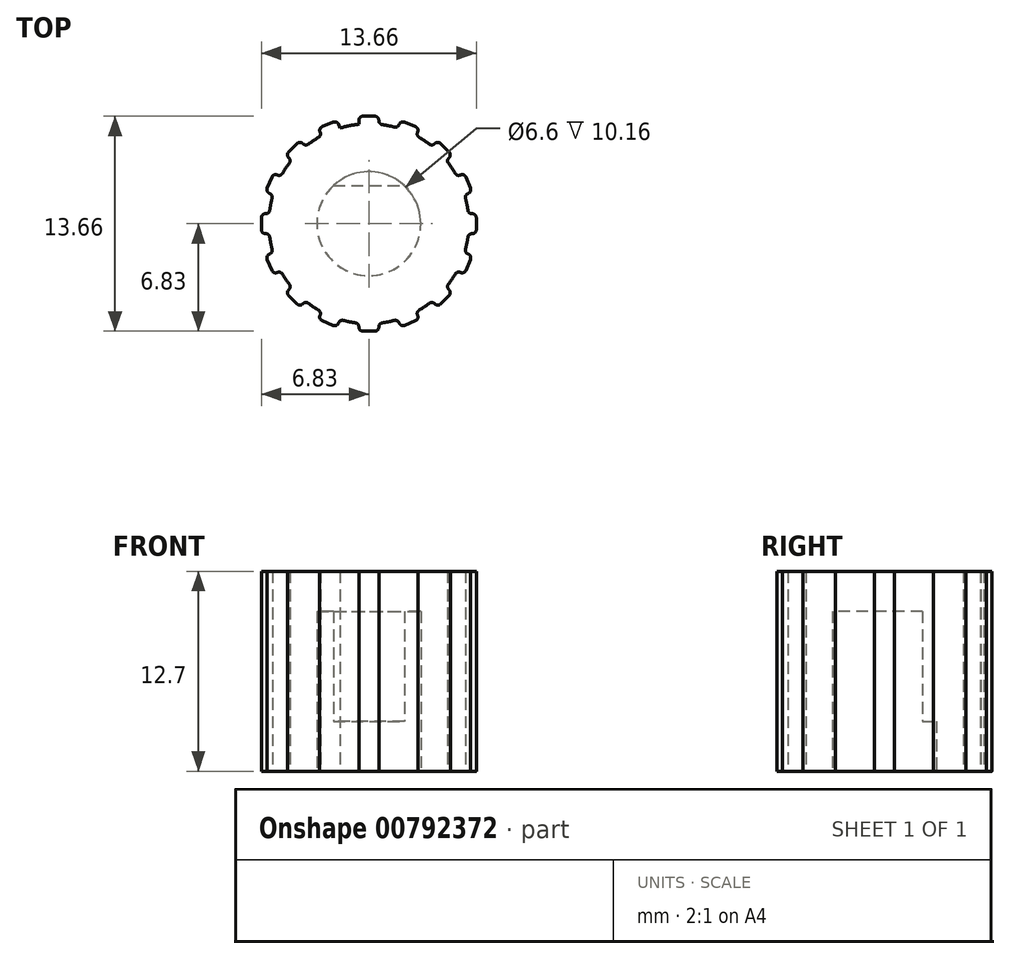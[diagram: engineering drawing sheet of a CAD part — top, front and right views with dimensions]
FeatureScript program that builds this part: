
annotation { "Feature Type Name" : "Feature", "Feature Type Description" : "" }
export const myFeature = defineFeature(function(context is Context, id is Id, definition is map)
    precondition{}
    {
        {
            var Q0;
            Q0=qCreatedBy(makeId("Top.planeOp"),FACE);
            var sketch = newSketch(context, id + "F0", { "sketchPlane" : qUnion([Q0])});
            skCircle(sketch, "E0", {"center": v(0, 0) * mm, "radius": 6.35 * mm});
            skSolve(sketch);
        }
        {
            var Q0;
            Q0 = qSketchRegion(id + "F0", true);
            extrude(context, id + "F1", {"entities" : qUnion([Q0]), "depth" : 12.7 * mm, "offsetDistance" : 25.4 * mm});
        }
        {
            var Q0;
            Q0=qCreatedBy(makeId("Top.planeOp"),FACE);
            var sketch = newSketch(context, id + "F2", { "sketchPlane" : qUnion([Q0])});
            skLineSegment(sketch, "E1", {"start": v(-0.63, 6.32) * mm, "end": v(-0.64, 6.83) * mm});
            skLineSegment(sketch, "E2", {"start": v(-0.64, 6.83) * mm, "end": v(0.64, 6.83) * mm});
            skLineSegment(sketch, "E3", {"start": v(0.64, 6.83) * mm, "end": v(0.64, 6.32) * mm});
            skLineSegment(sketch, "E4", {"start": v(0.64, 6.32) * mm, "end": v(-0.64, 6.32) * mm});
            skLineSegment(sketch, "E5.1.0", {"start": v(-3.2, 6.06) * mm, "end": v(-2.03, 6.55) * mm});
            skLineSegment(sketch, "E5.1.1", {"start": v(-3, 5.6) * mm, "end": v(-3.2, 6.06) * mm});
            skLineSegment(sketch, "E5.1.2", {"start": v(-1.83, 6.08) * mm, "end": v(-3, 5.6) * mm});
            skLineSegment(sketch, "E5.1.3", {"start": v(-2.03, 6.55) * mm, "end": v(-1.83, 6.08) * mm});
            skLineSegment(sketch, "E5.2.0", {"start": v(-5.28, 4.38) * mm, "end": v(-4.38, 5.28) * mm});
            skLineSegment(sketch, "E5.2.1", {"start": v(-4.92, 4.02) * mm, "end": v(-5.28, 4.38) * mm});
            skLineSegment(sketch, "E5.2.2", {"start": v(-4.02, 4.92) * mm, "end": v(-4.92, 4.02) * mm});
            skLineSegment(sketch, "E5.2.3", {"start": v(-4.38, 5.28) * mm, "end": v(-4.02, 4.92) * mm});
            skLineSegment(sketch, "E5.3.0", {"start": v(-6.55, 2.03) * mm, "end": v(-6.06, 3.2) * mm});
            skLineSegment(sketch, "E5.3.1", {"start": v(-6.08, 1.83) * mm, "end": v(-6.55, 2.03) * mm});
            skLineSegment(sketch, "E5.3.2", {"start": v(-5.6, 3) * mm, "end": v(-6.08, 1.83) * mm});
            skLineSegment(sketch, "E5.3.3", {"start": v(-6.06, 3.2) * mm, "end": v(-5.6, 3) * mm});
            skLineSegment(sketch, "E5.4.0", {"start": v(-6.83, -0.63) * mm, "end": v(-6.83, 0.64) * mm});
            skLineSegment(sketch, "E5.4.1", {"start": v(-6.32, -0.63) * mm, "end": v(-6.83, -0.63) * mm});
            skLineSegment(sketch, "E5.4.2", {"start": v(-6.32, 0.64) * mm, "end": v(-6.32, -0.63) * mm});
            skLineSegment(sketch, "E5.4.3", {"start": v(-6.83, 0.64) * mm, "end": v(-6.32, 0.64) * mm});
            skLineSegment(sketch, "E5.5.0", {"start": v(-6.06, -3.2) * mm, "end": v(-6.55, -2.03) * mm});
            skLineSegment(sketch, "E5.5.1", {"start": v(-5.6, -3) * mm, "end": v(-6.06, -3.2) * mm});
            skLineSegment(sketch, "E5.5.2", {"start": v(-6.08, -1.83) * mm, "end": v(-5.6, -3) * mm});
            skLineSegment(sketch, "E5.5.3", {"start": v(-6.55, -2.03) * mm, "end": v(-6.08, -1.83) * mm});
            skLineSegment(sketch, "E5.6.0", {"start": v(-4.38, -5.28) * mm, "end": v(-5.28, -4.38) * mm});
            skLineSegment(sketch, "E5.6.1", {"start": v(-4.02, -4.92) * mm, "end": v(-4.38, -5.28) * mm});
            skLineSegment(sketch, "E5.6.2", {"start": v(-4.92, -4.02) * mm, "end": v(-4.02, -4.92) * mm});
            skLineSegment(sketch, "E5.6.3", {"start": v(-5.28, -4.38) * mm, "end": v(-4.92, -4.02) * mm});
            skLineSegment(sketch, "E5.7.0", {"start": v(-2.03, -6.55) * mm, "end": v(-3.2, -6.06) * mm});
            skLineSegment(sketch, "E5.7.1", {"start": v(-1.83, -6.08) * mm, "end": v(-2.03, -6.55) * mm});
            skLineSegment(sketch, "E5.7.2", {"start": v(-3, -5.6) * mm, "end": v(-1.83, -6.08) * mm});
            skLineSegment(sketch, "E5.7.3", {"start": v(-3.2, -6.06) * mm, "end": v(-3, -5.6) * mm});
            skLineSegment(sketch, "E5.8.0", {"start": v(0.63, -6.83) * mm, "end": v(-0.64, -6.83) * mm});
            skLineSegment(sketch, "E5.8.1", {"start": v(0.63, -6.32) * mm, "end": v(0.63, -6.83) * mm});
            skLineSegment(sketch, "E5.8.2", {"start": v(-0.64, -6.32) * mm, "end": v(0.63, -6.32) * mm});
            skLineSegment(sketch, "E5.8.3", {"start": v(-0.64, -6.83) * mm, "end": v(-0.64, -6.32) * mm});
            skLineSegment(sketch, "E5.9.0", {"start": v(3.2, -6.06) * mm, "end": v(2.03, -6.55) * mm});
            skLineSegment(sketch, "E5.9.1", {"start": v(3, -5.6) * mm, "end": v(3.2, -6.06) * mm});
            skLineSegment(sketch, "E5.9.2", {"start": v(1.83, -6.08) * mm, "end": v(3, -5.6) * mm});
            skLineSegment(sketch, "E5.9.3", {"start": v(2.03, -6.55) * mm, "end": v(1.83, -6.08) * mm});
            skLineSegment(sketch, "E5.10.0", {"start": v(5.28, -4.38) * mm, "end": v(4.38, -5.28) * mm});
            skLineSegment(sketch, "E5.10.1", {"start": v(4.92, -4.02) * mm, "end": v(5.28, -4.38) * mm});
            skLineSegment(sketch, "E5.10.2", {"start": v(4.02, -4.92) * mm, "end": v(4.92, -4.02) * mm});
            skLineSegment(sketch, "E5.10.3", {"start": v(4.38, -5.28) * mm, "end": v(4.02, -4.92) * mm});
            skLineSegment(sketch, "E5.11.0", {"start": v(6.55, -2.03) * mm, "end": v(6.06, -3.2) * mm});
            skLineSegment(sketch, "E5.11.1", {"start": v(6.08, -1.83) * mm, "end": v(6.55, -2.03) * mm});
            skLineSegment(sketch, "E5.11.2", {"start": v(5.6, -3) * mm, "end": v(6.08, -1.83) * mm});
            skLineSegment(sketch, "E5.11.3", {"start": v(6.06, -3.2) * mm, "end": v(5.6, -3) * mm});
            skLineSegment(sketch, "E5.12.0", {"start": v(6.83, 0.63) * mm, "end": v(6.83, -0.64) * mm});
            skLineSegment(sketch, "E5.12.1", {"start": v(6.32, 0.63) * mm, "end": v(6.83, 0.63) * mm});
            skLineSegment(sketch, "E5.12.2", {"start": v(6.32, -0.64) * mm, "end": v(6.32, 0.63) * mm});
            skLineSegment(sketch, "E5.12.3", {"start": v(6.83, -0.64) * mm, "end": v(6.32, -0.64) * mm});
            skLineSegment(sketch, "E5.13.0", {"start": v(6.06, 3.2) * mm, "end": v(6.55, 2.03) * mm});
            skLineSegment(sketch, "E5.13.1", {"start": v(5.6, 3) * mm, "end": v(6.06, 3.2) * mm});
            skLineSegment(sketch, "E5.13.2", {"start": v(6.08, 1.83) * mm, "end": v(5.6, 3) * mm});
            skLineSegment(sketch, "E5.13.3", {"start": v(6.55, 2.03) * mm, "end": v(6.08, 1.83) * mm});
            skLineSegment(sketch, "E5.14.0", {"start": v(4.38, 5.28) * mm, "end": v(5.28, 4.38) * mm});
            skLineSegment(sketch, "E5.14.1", {"start": v(4.02, 4.92) * mm, "end": v(4.38, 5.28) * mm});
            skLineSegment(sketch, "E5.14.2", {"start": v(4.92, 4.02) * mm, "end": v(4.02, 4.92) * mm});
            skLineSegment(sketch, "E5.14.3", {"start": v(5.28, 4.38) * mm, "end": v(4.92, 4.02) * mm});
            skLineSegment(sketch, "E5.15.0", {"start": v(2.03, 6.55) * mm, "end": v(3.2, 6.06) * mm});
            skLineSegment(sketch, "E5.15.1", {"start": v(1.83, 6.08) * mm, "end": v(2.03, 6.55) * mm});
            skLineSegment(sketch, "E5.15.2", {"start": v(3, 5.6) * mm, "end": v(1.83, 6.08) * mm});
            skLineSegment(sketch, "E5.15.3", {"start": v(3.2, 6.06) * mm, "end": v(3, 5.6) * mm});
            skPoint(sketch, "E5.center", {"position": v(0, 0) * mm});
            skSolve(sketch);
        }
        {
            var Q0;
            Q0 = qSketchRegion(id + "F2", true);
            var Q1;
            Q1=makeQuery(id+"F1.opExtrude","CAP_FACE",FACE,{"disambiguationData":[OSD([sQuery(id+"F0.wireOp",EDGE,"E0")])],"isStart":false});
            extrude(context, id + "F3", {"entities" : qUnion([Q0]), "operationType" : NewBodyOperationType.ADD, "endBound" : BoundingType.UP_TO_SURFACE, "depth" : 25.4 * mm, "endBoundEntityFace" : qUnion([Q1]), "offsetDistance" : 25.4 * mm});
        }
        {
            var Q0;
            Q0=makeQuery(id+"F3.opExtrude","SWEPT_EDGE",EDGE,{"disambiguationData":[OSD([sQuery(id+"F2.wireOp",EDGE,"E2"),sQuery(id+"F2.wireOp",EDGE,"E3")])]});
            var Q1;
            Q1=makeQuery(id+"F3.opExtrude","SWEPT_EDGE",EDGE,{"disambiguationData":[OSD([sQuery(id+"F2.wireOp",EDGE,"E1"),sQuery(id+"F2.wireOp",EDGE,"E2")])]});
            var Q2;
            Q2=makeQuery(id+"F3.opExtrude","SWEPT_EDGE",EDGE,{"disambiguationData":[OSD([sQuery(id+"F2.wireOp",EDGE,"E3"),sQuery(id+"F2.wireOp",EDGE,"E4")])]});
            var Q3;
            Q3=makeQuery(id+"F3.opExtrude","SWEPT_EDGE",EDGE,{"disambiguationData":[OSD([sQuery(id+"F2.wireOp",EDGE,"E1"),sQuery(id+"F2.wireOp",EDGE,"E4")])]});
            var Q4;
            Q4=makeQuery(id+"F3.opExtrude","SWEPT_EDGE",EDGE,{"disambiguationData":[OSD([sQuery(id+"F2.wireOp",EDGE,"E5.15.1"),sQuery(id+"F2.wireOp",EDGE,"E5.15.2")])]});
            var Q5;
            Q5=makeQuery(id+"F3.opExtrude","SWEPT_EDGE",EDGE,{"disambiguationData":[OSD([sQuery(id+"F2.wireOp",EDGE,"E5.15.0"),sQuery(id+"F2.wireOp",EDGE,"E5.15.1")])]});
            var Q6;
            Q6=makeQuery(id+"F3.opExtrude","SWEPT_EDGE",EDGE,{"disambiguationData":[OSD([sQuery(id+"F2.wireOp",EDGE,"E5.15.0"),sQuery(id+"F2.wireOp",EDGE,"E5.15.3")])]});
            var Q7;
            Q7=makeQuery(id+"F3.opExtrude","SWEPT_EDGE",EDGE,{"disambiguationData":[OSD([sQuery(id+"F2.wireOp",EDGE,"E5.15.2"),sQuery(id+"F2.wireOp",EDGE,"E5.15.3")])]});
            var Q8;
            Q8=makeQuery(id+"F3.opExtrude","SWEPT_EDGE",EDGE,{"disambiguationData":[OSD([sQuery(id+"F2.wireOp",EDGE,"E5.14.0"),sQuery(id+"F2.wireOp",EDGE,"E5.14.1")])]});
            var Q9;
            Q9=makeQuery(id+"F3.opExtrude","SWEPT_EDGE",EDGE,{"disambiguationData":[OSD([sQuery(id+"F2.wireOp",EDGE,"E5.14.0"),sQuery(id+"F2.wireOp",EDGE,"E5.14.3")])]});
            var Q10;
            Q10=makeQuery(id+"F3.opExtrude","SWEPT_EDGE",EDGE,{"disambiguationData":[OSD([sQuery(id+"F2.wireOp",EDGE,"E5.14.1"),sQuery(id+"F2.wireOp",EDGE,"E5.14.2")])]});
            var Q11;
            Q11=makeQuery(id+"F3.opExtrude","SWEPT_EDGE",EDGE,{"disambiguationData":[OSD([sQuery(id+"F2.wireOp",EDGE,"E5.14.2"),sQuery(id+"F2.wireOp",EDGE,"E5.14.3")])]});
            var Q12;
            Q12=makeQuery(id+"F3.opExtrude","SWEPT_EDGE",EDGE,{"disambiguationData":[OSD([sQuery(id+"F2.wireOp",EDGE,"E5.13.1"),sQuery(id+"F2.wireOp",EDGE,"E5.13.2")])]});
            var Q13;
            Q13=makeQuery(id+"F3.opExtrude","SWEPT_EDGE",EDGE,{"disambiguationData":[OSD([sQuery(id+"F2.wireOp",EDGE,"E5.13.0"),sQuery(id+"F2.wireOp",EDGE,"E5.13.1")])]});
            var Q14;
            Q14=makeQuery(id+"F3.opExtrude","SWEPT_EDGE",EDGE,{"disambiguationData":[OSD([sQuery(id+"F2.wireOp",EDGE,"E5.13.0"),sQuery(id+"F2.wireOp",EDGE,"E5.13.3")])]});
            var Q15;
            Q15=makeQuery(id+"F3.opExtrude","SWEPT_EDGE",EDGE,{"disambiguationData":[OSD([sQuery(id+"F2.wireOp",EDGE,"E5.13.2"),sQuery(id+"F2.wireOp",EDGE,"E5.13.3")])]});
            var Q16;
            Q16=makeQuery(id+"F3.opExtrude","SWEPT_EDGE",EDGE,{"disambiguationData":[OSD([sQuery(id+"F2.wireOp",EDGE,"E5.12.0"),sQuery(id+"F2.wireOp",EDGE,"E5.12.1")])]});
            var Q17;
            Q17=makeQuery(id+"F3.opExtrude","SWEPT_EDGE",EDGE,{"disambiguationData":[OSD([sQuery(id+"F2.wireOp",EDGE,"E5.12.1"),sQuery(id+"F2.wireOp",EDGE,"E5.12.2")])]});
            var Q18;
            Q18=makeQuery(id+"F3.opExtrude","SWEPT_EDGE",EDGE,{"disambiguationData":[OSD([sQuery(id+"F2.wireOp",EDGE,"E5.12.0"),sQuery(id+"F2.wireOp",EDGE,"E5.12.3")])]});
            var Q19;
            Q19=makeQuery(id+"F3.opExtrude","SWEPT_EDGE",EDGE,{"disambiguationData":[OSD([sQuery(id+"F2.wireOp",EDGE,"E5.12.2"),sQuery(id+"F2.wireOp",EDGE,"E5.12.3")])]});
            var Q20;
            Q20=makeQuery(id+"F3.opExtrude","SWEPT_EDGE",EDGE,{"disambiguationData":[OSD([sQuery(id+"F2.wireOp",EDGE,"E5.11.0"),sQuery(id+"F2.wireOp",EDGE,"E5.11.1")])]});
            var Q21;
            Q21=makeQuery(id+"F3.opExtrude","SWEPT_EDGE",EDGE,{"disambiguationData":[OSD([sQuery(id+"F2.wireOp",EDGE,"E5.11.1"),sQuery(id+"F2.wireOp",EDGE,"E5.11.2")])]});
            var Q22;
            Q22=makeQuery(id+"F3.opExtrude","SWEPT_EDGE",EDGE,{"disambiguationData":[OSD([sQuery(id+"F2.wireOp",EDGE,"E5.11.0"),sQuery(id+"F2.wireOp",EDGE,"E5.11.3")])]});
            var Q23;
            Q23=makeQuery(id+"F3.opExtrude","SWEPT_EDGE",EDGE,{"disambiguationData":[OSD([sQuery(id+"F2.wireOp",EDGE,"E5.10.0"),sQuery(id+"F2.wireOp",EDGE,"E5.10.1")])]});
            var Q24;
            Q24=makeQuery(id+"F3.opExtrude","SWEPT_EDGE",EDGE,{"disambiguationData":[OSD([sQuery(id+"F2.wireOp",EDGE,"E5.11.2"),sQuery(id+"F2.wireOp",EDGE,"E5.11.3")])]});
            var Q25;
            Q25=makeQuery(id+"F3.opExtrude","SWEPT_EDGE",EDGE,{"disambiguationData":[OSD([sQuery(id+"F2.wireOp",EDGE,"E5.10.1"),sQuery(id+"F2.wireOp",EDGE,"E5.10.2")])]});
            var Q26;
            Q26=makeQuery(id+"F3.opExtrude","SWEPT_EDGE",EDGE,{"disambiguationData":[OSD([sQuery(id+"F2.wireOp",EDGE,"E5.10.0"),sQuery(id+"F2.wireOp",EDGE,"E5.10.3")])]});
            var Q27;
            Q27=makeQuery(id+"F3.opExtrude","SWEPT_EDGE",EDGE,{"disambiguationData":[OSD([sQuery(id+"F2.wireOp",EDGE,"E5.10.2"),sQuery(id+"F2.wireOp",EDGE,"E5.10.3")])]});
            var Q28;
            Q28=makeQuery(id+"F3.opExtrude","SWEPT_EDGE",EDGE,{"disambiguationData":[OSD([sQuery(id+"F2.wireOp",EDGE,"E5.9.1"),sQuery(id+"F2.wireOp",EDGE,"E5.9.2")])]});
            var Q29;
            Q29=makeQuery(id+"F3.opExtrude","SWEPT_EDGE",EDGE,{"disambiguationData":[OSD([sQuery(id+"F2.wireOp",EDGE,"E5.9.0"),sQuery(id+"F2.wireOp",EDGE,"E5.9.1")])]});
            var Q30;
            Q30=makeQuery(id+"F3.opExtrude","SWEPT_EDGE",EDGE,{"disambiguationData":[OSD([sQuery(id+"F2.wireOp",EDGE,"E5.8.1"),sQuery(id+"F2.wireOp",EDGE,"E5.8.2")])]});
            var Q31;
            Q31=makeQuery(id+"F3.opExtrude","SWEPT_EDGE",EDGE,{"disambiguationData":[OSD([sQuery(id+"F2.wireOp",EDGE,"E5.8.0"),sQuery(id+"F2.wireOp",EDGE,"E5.8.1")])]});
            var Q32;
            Q32=makeQuery(id+"F3.opExtrude","SWEPT_EDGE",EDGE,{"disambiguationData":[OSD([sQuery(id+"F2.wireOp",EDGE,"E5.9.2"),sQuery(id+"F2.wireOp",EDGE,"E5.9.3")])]});
            var Q33;
            Q33=makeQuery(id+"F3.opExtrude","SWEPT_EDGE",EDGE,{"disambiguationData":[OSD([sQuery(id+"F2.wireOp",EDGE,"E5.9.0"),sQuery(id+"F2.wireOp",EDGE,"E5.9.3")])]});
            var Q34;
            Q34=makeQuery(id+"F3.opExtrude","SWEPT_EDGE",EDGE,{"disambiguationData":[OSD([sQuery(id+"F2.wireOp",EDGE,"E5.8.0"),sQuery(id+"F2.wireOp",EDGE,"E5.8.3")])]});
            var Q35;
            Q35=makeQuery(id+"F3.opExtrude","SWEPT_EDGE",EDGE,{"disambiguationData":[OSD([sQuery(id+"F2.wireOp",EDGE,"E5.8.2"),sQuery(id+"F2.wireOp",EDGE,"E5.8.3")])]});
            var Q36;
            Q36=makeQuery(id+"F3.opExtrude","SWEPT_EDGE",EDGE,{"disambiguationData":[OSD([sQuery(id+"F2.wireOp",EDGE,"E5.7.1"),sQuery(id+"F2.wireOp",EDGE,"E5.7.2")])]});
            var Q37;
            Q37=makeQuery(id+"F3.opExtrude","SWEPT_EDGE",EDGE,{"disambiguationData":[OSD([sQuery(id+"F2.wireOp",EDGE,"E5.7.0"),sQuery(id+"F2.wireOp",EDGE,"E5.7.1")])]});
            var Q38;
            Q38=makeQuery(id+"F3.opExtrude","SWEPT_EDGE",EDGE,{"disambiguationData":[OSD([sQuery(id+"F2.wireOp",EDGE,"E5.7.0"),sQuery(id+"F2.wireOp",EDGE,"E5.7.3")])]});
            var Q39;
            Q39=makeQuery(id+"F3.opExtrude","SWEPT_EDGE",EDGE,{"disambiguationData":[OSD([sQuery(id+"F2.wireOp",EDGE,"E5.7.2"),sQuery(id+"F2.wireOp",EDGE,"E5.7.3")])]});
            var Q40;
            Q40=makeQuery(id+"F3.opExtrude","SWEPT_EDGE",EDGE,{"disambiguationData":[OSD([sQuery(id+"F2.wireOp",EDGE,"E5.6.1"),sQuery(id+"F2.wireOp",EDGE,"E5.6.2")])]});
            var Q41;
            Q41=makeQuery(id+"F3.opExtrude","SWEPT_EDGE",EDGE,{"disambiguationData":[OSD([sQuery(id+"F2.wireOp",EDGE,"E5.6.0"),sQuery(id+"F2.wireOp",EDGE,"E5.6.1")])]});
            var Q42;
            Q42=makeQuery(id+"F3.opExtrude","SWEPT_EDGE",EDGE,{"disambiguationData":[OSD([sQuery(id+"F2.wireOp",EDGE,"E5.5.1"),sQuery(id+"F2.wireOp",EDGE,"E5.5.2")])]});
            var Q43;
            Q43=makeQuery(id+"F3.opExtrude","SWEPT_EDGE",EDGE,{"disambiguationData":[OSD([sQuery(id+"F2.wireOp",EDGE,"E5.5.0"),sQuery(id+"F2.wireOp",EDGE,"E5.5.1")])]});
            var Q44;
            Q44=makeQuery(id+"F3.opExtrude","SWEPT_EDGE",EDGE,{"disambiguationData":[OSD([sQuery(id+"F2.wireOp",EDGE,"E5.6.0"),sQuery(id+"F2.wireOp",EDGE,"E5.6.3")])]});
            var Q45;
            Q45=makeQuery(id+"F3.opExtrude","SWEPT_EDGE",EDGE,{"disambiguationData":[OSD([sQuery(id+"F2.wireOp",EDGE,"E5.6.2"),sQuery(id+"F2.wireOp",EDGE,"E5.6.3")])]});
            var Q46;
            Q46=makeQuery(id+"F3.opExtrude","SWEPT_EDGE",EDGE,{"disambiguationData":[OSD([sQuery(id+"F2.wireOp",EDGE,"E5.5.2"),sQuery(id+"F2.wireOp",EDGE,"E5.5.3")])]});
            var Q47;
            Q47=makeQuery(id+"F3.opExtrude","SWEPT_EDGE",EDGE,{"disambiguationData":[OSD([sQuery(id+"F2.wireOp",EDGE,"E5.5.0"),sQuery(id+"F2.wireOp",EDGE,"E5.5.3")])]});
            var Q48;
            Q48=makeQuery(id+"F3.opExtrude","SWEPT_EDGE",EDGE,{"disambiguationData":[OSD([sQuery(id+"F2.wireOp",EDGE,"E5.4.1"),sQuery(id+"F2.wireOp",EDGE,"E5.4.2")])]});
            var Q49;
            Q49=makeQuery(id+"F3.opExtrude","SWEPT_EDGE",EDGE,{"disambiguationData":[OSD([sQuery(id+"F2.wireOp",EDGE,"E5.4.0"),sQuery(id+"F2.wireOp",EDGE,"E5.4.1")])]});
            var Q50;
            Q50=makeQuery(id+"F3.opExtrude","SWEPT_EDGE",EDGE,{"disambiguationData":[OSD([sQuery(id+"F2.wireOp",EDGE,"E5.4.0"),sQuery(id+"F2.wireOp",EDGE,"E5.4.3")])]});
            var Q51;
            Q51=makeQuery(id+"F3.opExtrude","SWEPT_EDGE",EDGE,{"disambiguationData":[OSD([sQuery(id+"F2.wireOp",EDGE,"E5.4.2"),sQuery(id+"F2.wireOp",EDGE,"E5.4.3")])]});
            var Q52;
            Q52=makeQuery(id+"F3.opExtrude","SWEPT_EDGE",EDGE,{"disambiguationData":[OSD([sQuery(id+"F2.wireOp",EDGE,"E5.3.1"),sQuery(id+"F2.wireOp",EDGE,"E5.3.2")])]});
            var Q53;
            Q53=makeQuery(id+"F3.opExtrude","SWEPT_EDGE",EDGE,{"disambiguationData":[OSD([sQuery(id+"F2.wireOp",EDGE,"E5.3.0"),sQuery(id+"F2.wireOp",EDGE,"E5.3.1")])]});
            var Q54;
            Q54=makeQuery(id+"F3.opExtrude","SWEPT_EDGE",EDGE,{"disambiguationData":[OSD([sQuery(id+"F2.wireOp",EDGE,"E5.3.0"),sQuery(id+"F2.wireOp",EDGE,"E5.3.3")])]});
            var Q55;
            Q55=makeQuery(id+"F3.opExtrude","SWEPT_EDGE",EDGE,{"disambiguationData":[OSD([sQuery(id+"F2.wireOp",EDGE,"E5.3.2"),sQuery(id+"F2.wireOp",EDGE,"E5.3.3")])]});
            var Q56;
            Q56=makeQuery(id+"F3.opExtrude","SWEPT_EDGE",EDGE,{"disambiguationData":[OSD([sQuery(id+"F2.wireOp",EDGE,"E5.2.0"),sQuery(id+"F2.wireOp",EDGE,"E5.2.3")])]});
            var Q57;
            Q57=makeQuery(id+"F3.opExtrude","SWEPT_EDGE",EDGE,{"disambiguationData":[OSD([sQuery(id+"F2.wireOp",EDGE,"E5.2.2"),sQuery(id+"F2.wireOp",EDGE,"E5.2.3")])]});
            var Q58;
            Q58=makeQuery(id+"F3.opExtrude","SWEPT_EDGE",EDGE,{"disambiguationData":[OSD([sQuery(id+"F2.wireOp",EDGE,"E5.2.1"),sQuery(id+"F2.wireOp",EDGE,"E5.2.2")])]});
            var Q59;
            Q59=makeQuery(id+"F3.opExtrude","SWEPT_EDGE",EDGE,{"disambiguationData":[OSD([sQuery(id+"F2.wireOp",EDGE,"E5.2.0"),sQuery(id+"F2.wireOp",EDGE,"E5.2.1")])]});
            var Q60;
            Q60=makeQuery(id+"F3.opExtrude","SWEPT_EDGE",EDGE,{"disambiguationData":[OSD([sQuery(id+"F2.wireOp",EDGE,"E5.1.2"),sQuery(id+"F2.wireOp",EDGE,"E5.1.3")])]});
            var Q61;
            Q61=makeQuery(id+"F3.opExtrude","SWEPT_EDGE",EDGE,{"disambiguationData":[OSD([sQuery(id+"F2.wireOp",EDGE,"E5.1.0"),sQuery(id+"F2.wireOp",EDGE,"E5.1.3")])]});
            var Q62;
            Q62=makeQuery(id+"F3.opExtrude","SWEPT_EDGE",EDGE,{"disambiguationData":[OSD([sQuery(id+"F2.wireOp",EDGE,"E5.1.1"),sQuery(id+"F2.wireOp",EDGE,"E5.1.2")])]});
            var Q63;
            Q63=makeQuery(id+"F3.opExtrude","SWEPT_EDGE",EDGE,{"disambiguationData":[OSD([sQuery(id+"F2.wireOp",EDGE,"E5.1.0"),sQuery(id+"F2.wireOp",EDGE,"E5.1.1")])]});
            fillet(context, id + "F4", {"entities" : qUnion([Q0, Q1, Q2, Q3, Q4, Q5, Q6, Q7, Q8, Q9, Q10, Q11, Q12, Q13, Q14, Q15, Q16, Q17, Q18, Q19, Q20, Q21, Q22, Q23, Q24, Q25, Q26, Q27, Q28, Q29, Q30, Q31, Q32, Q33, Q34, Q35, Q36, Q37, Q38, Q39, Q40, Q41, Q42, Q43, Q44, Q45, Q46, Q47, Q48, Q49, Q50, Q51, Q52, Q53, Q54, Q55, Q56, Q57, Q58, Q59, Q60, Q61, Q62, Q63]), "radius" : 0.25 * mm, "tangentPropagation" : true, "allowEdgeOverflow" : false});
        }
        {
            var Q0;
            Q0=qCreatedBy(makeId("Top.planeOp"),FACE);
            var sketch = newSketch(context, id + "F5", { "sketchPlane" : qUnion([Q0])});
            skArc(sketch, "E6", {"start": v(-2.25, 2.41) * mm, "mid": v(0, -3.3) * mm, "end": v(2.25, 2.41) * mm});
            skLineSegment(sketch, "E7", {"start": v(-2.25, 2.41) * mm, "end": v(2.25, 2.41) * mm});
            skSolve(sketch);
        }
        {
            var Q0;
            Q0 = qSketchRegion(id + "F5", true);
            extrude(context, id + "F6", {"entities" : qUnion([Q0]), "operationType" : NewBodyOperationType.REMOVE, "depth" : 10.16 * mm, "offsetDistance" : 25.4 * mm});
        }
        {
            var Q0;
            Q0=qCreatedBy(makeId("Top.planeOp"),FACE);
            var sketch = newSketch(context, id + "F7", { "sketchPlane" : qUnion([Q0])});
            skCircle(sketch, "E8", {"center": v(0, 0) * mm, "radius": 3.3 * mm});
            skSolve(sketch);
        }
        {
            var Q0;
            Q0 = qSketchRegion(id + "F7", true);
            extrude(context, id + "F8", {"entities" : qUnion([Q0]), "operationType" : NewBodyOperationType.REMOVE, "depth" : 3.17 * mm, "offsetDistance" : 25.4 * mm});
        }
    });
